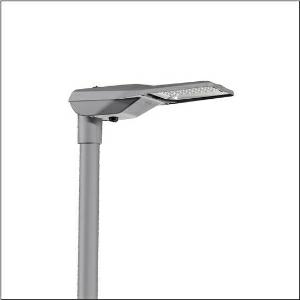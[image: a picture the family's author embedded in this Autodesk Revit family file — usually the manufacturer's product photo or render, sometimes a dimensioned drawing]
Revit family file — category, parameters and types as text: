
# Revit family: streetlight_sl_21_iq_mini___st1_0a_5xe2d31y08jb_55ca
name_source: partatom
category: Lighting Fixtures
units: mm (PartAtom-declared; Revit-internal decimal feet)

## family parameters
Cut with Voids When Loaded = No
Host = Face
Light Source = No
Part Type = Normal
Room Calculation Point = No
Round Connector Dimension = Use Diameter
Shared = No

## types (1)
- --- (1 x LED, 11210 lm, 72.5 W, 3000K)
    Apparent Load = 73 VA
    CIE Flux Codes = 40 73 97 100 100
    Color Rendering = 70
    Color Temperature = 3000K
    Default Elevation = 1800 mm
    Description = Streetlight SL 21 iQ mini, mast luminaire, primary light control with lens, of PMMA, primary optical cover: cover, of toughened safety glass, transparent, light distribution: ST1.0a, light emission: direct distribution, primary light characteristic: asymmetric, installation type: post-top, side-entry, LED, High Power LED, rated luminous flux: 11.210lm, luminous efficacy: 155lm/W, light colour: 730, colour temperature: 3000K, control gear: iQ-Street Remote, D4i with power reduction, control: pre-setting: logarithmic dimming characteristic, Street-Remote, Auto-Match, Temp-Guard, Lumen-Switch, Night-Set, Smart-Wire, Light-Fading, Desk-Remote (wireless, voltage-free reading and setting of iQ features in the workshop via application-optimized NFC function/RFID function), optimised constant luminous flux control (CLO 2.0), mains connection: 220..240V, AC, 50/60Hz, start of lifetime: 73W, end of service life: 76W, reduction: 33W, luminaire housing, of diecast aluminium, powder-coated, SITECO metallic grey (DB 702S), corrosivity category C5 high according to DIN EN ISO 12944, please order mast flange separately, inclination adjustable: 0°, 5°, 10°, 15°, sealing non-destructively replaceable, multi-level sealing system, length: 628mm, width: 235mm, height: 110mm, mast flange for spigot size: 42mm (side-entry): 5XC10008XM4, 60/48mm (side-entry/post-top): 5XC10108XM2, 76/60mm (side-entry/post-top): 5XC10108XM1, mounting height: 4..8m, Smart Interface below and above, protection rating (complete): IP66, insulation class (complete): insulation class II (safety insulation), certification: CE, ENEC, ENEC+, VDE, impact resistance: IK10, permissible operating ambient temperature for outdoor applications: -40..+50°C, standard-compliant lighting for roads and squares, packaging unit: 1 piece

Light Distribution: ST1.0a
    Height = 110 mm
    Lamp = 1 x LED
    Lamp Light Flux = 11210 lm
    Lamp Power = 72.5 W
    Lamp count = 1
    Length = 625 mm
    Luminous efficacy = 155 lm/W
    Manufacturer = Siteco
    ModVariant = No
    Model = 5XE2D31Y08JB
    Number of Poles = 1
    OnlyDefault = Yes
    Power Factor = 1
    Product Name = Streetlight SL 21 iQ mini | ST1.0a
    Product group = mast luminaire | pylon top
    ProductGroupID = 6100
    Protection Class = Protection class II
    Protection Degree = IP 66
    RLX_Detail_Level = 1
    RLX_Emergency_Light_Flux = 0 lm
    RLX_Emergency_Type = 0
    RLX_Emergency_Type_DB = No
    RlxData = <blob elided: 94485 chars, md5=1eed1eeb>
    Socket = socket
    Standby Power = 0 W
    System Light Flux = 11210 lm
    System Power = 73 W
    Type Comments = factory setting: luminous flux: 100 % | dim-lin: 254 | 755 mA
    Type Image = l_1003514.jpg
    URL = http://relux.com
    VarID = @adj_114195
    Voltage = 0 V
    Weight = 0.00 kg
    Width = 234 mm

## geometry (parser evidence)
native form markers: Blend x4, Sweep x10
no freeform markers — native parametric forms only
